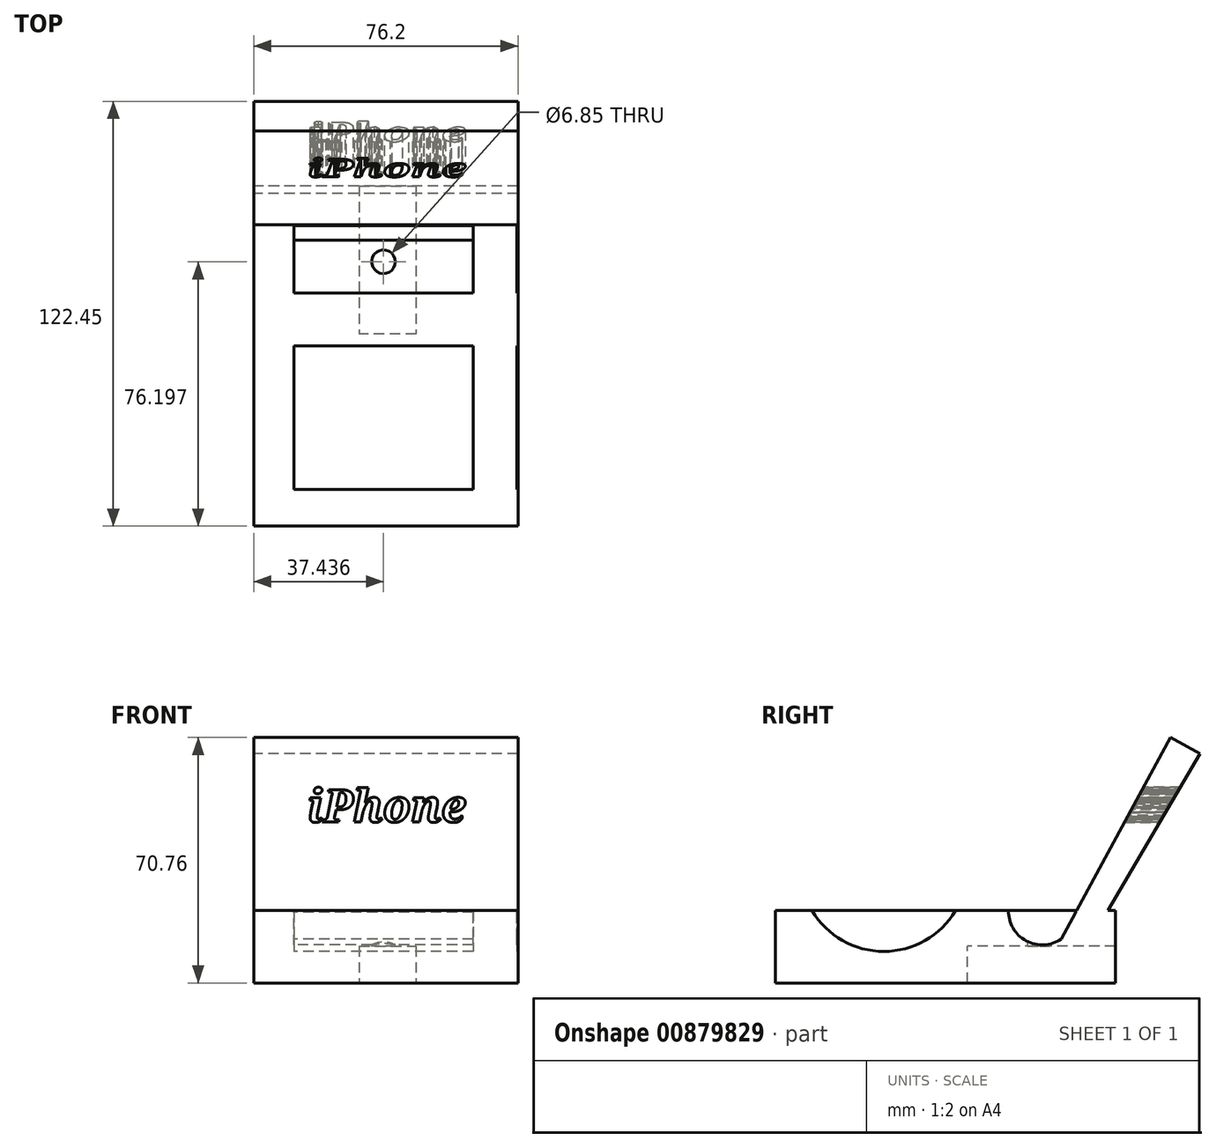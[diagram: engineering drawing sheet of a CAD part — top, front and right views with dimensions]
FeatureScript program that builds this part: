
annotation { "Feature Type Name" : "Feature", "Feature Type Description" : "" }
export const myFeature = defineFeature(function(context is Context, id is Id, definition is map)
    precondition{}
    {
        {
            var Q0;
            Q0=qCreatedBy(makeId("Right.planeOp"),FACE);
            var sketch = newSketch(context, id + "F0", { "sketchPlane" : qUnion([Q0])});
            skLineSegment(sketch, "E0.bottom", {"start": v(42.72, 0) * mm, "end": v(40.53, 0) * mm});
            skLineSegment(sketch, "E0.top", {"start": v(42.72, -20.85) * mm, "end": v(-55.35, -20.85) * mm});
            skLineSegment(sketch, "E0.left", {"start": v(42.72, 0) * mm, "end": v(42.72, -20.85) * mm});
            skLineSegment(sketch, "E0.right", {"start": v(-55.35, 0) * mm, "end": v(-55.35, -20.85) * mm});
            skArc(sketch, "E1", {"start": v(11.9, 0) * mm, "mid": v(16.98, -8.72) * mm, "end": v(27.06, -8.2) * mm});
            skLineSegment(sketch, "E2.trimOffspring", {"start": v(11.9, 0) * mm, "end": v(-3.38, 0) * mm});
            skArc(sketch, "E3", {"start": v(-44.78, 0) * mm, "mid": v(-24.08, -11.77) * mm, "end": v(-3.38, 0) * mm});
            skLineSegment(sketch, "E4", {"start": v(27.06, -8.2) * mm, "end": v(58.58, 49.91) * mm});
            skLineSegment(sketch, "E5", {"start": v(58.58, 49.91) * mm, "end": v(67.1, 45.29) * mm});
            skLineSegment(sketch, "E6", {"start": v(67.1, 45.29) * mm, "end": v(40.53, 0) * mm});
            skArc(sketch, "E7.trimOffspring", {"start": v(31.27, -0.43) * mm, "mid": v(31.27, -0.21) * mm, "end": v(31.27, 0) * mm});
            skLineSegment(sketch, "E8.trimOffspring", {"start": v(31.5, 0) * mm, "end": v(31.27, 0) * mm});
            skLineSegment(sketch, "E9.trimOffspring", {"start": v(-44.78, 0) * mm, "end": v(-55.35, 0) * mm});
            skSolve(sketch);
        }
        {
            var Q0;
            Q0 = qSketchRegion(id + "F0", true);
            extrude(context, id + "F1", {"entities" : qUnion([Q0]), "depth" : 76.2 * mm, "offsetDistance" : 25.4 * mm});
        }
        {
            var Q0;
            Q0=qCreatedBy(makeId("Top.planeOp"),FACE);
            var sketch = newSketch(context, id + "F2", { "sketchPlane" : qUnion([Q0])});
            skLineSegment(sketch, "E10.bottom", {"start": v(0, 32) * mm, "end": v(11.6, 32) * mm});
            skLineSegment(sketch, "E10.top", {"start": v(0, -55.2) * mm, "end": v(11.6, -55.2) * mm});
            skLineSegment(sketch, "E10.left", {"start": v(0, 32) * mm, "end": v(0, -55.2) * mm});
            skLineSegment(sketch, "E10.right", {"start": v(11.6, 32) * mm, "end": v(11.6, -55.2) * mm});
            skLineSegment(sketch, "E11.bottom", {"start": v(75.9, -55.2) * mm, "end": v(63.27, -55.2) * mm});
            skLineSegment(sketch, "E11.top", {"start": v(75.9, 32) * mm, "end": v(63.27, 32) * mm});
            skLineSegment(sketch, "E11.left", {"start": v(75.9, -55.2) * mm, "end": v(75.9, 32) * mm});
            skLineSegment(sketch, "E11.right", {"start": v(63.27, -55.2) * mm, "end": v(63.27, 32) * mm});
            skSolve(sketch);
        }
        {
            var Q0;
            Q0 = qSketchRegion(id + "F2", true);
            extrude(context, id + "F3", {"entities" : qUnion([Q0]), "operationType" : NewBodyOperationType.ADD, "oppositeDirection" : true, "depth" : 20.32 * mm, "offsetDistance" : 25.4 * mm});
        }
        {
            var Q0;
            Q0=qCreatedBy(makeId("Top.planeOp"),FACE);
            var sketch = newSketch(context, id + "F4", { "sketchPlane" : qUnion([Q0])});
            skCircle(sketch, "E12", {"center": v(37.44, 20.85) * mm, "radius": 3.42 * mm});
            skSolve(sketch);
        }
        {
            var Q0;
            Q0 = qSketchRegion(id + "F4", true);
            extrude(context, id + "F5", {"entities" : qUnion([Q0]), "operationType" : NewBodyOperationType.REMOVE, "oppositeDirection" : true, "depth" : 177.8 * mm, "offsetDistance" : 25.4 * mm});
        }
        {
            var Q0;
            Q0=qCreatedBy(makeId("Front.planeOp"),FACE);
            var sketch = newSketch(context, id + "F6", { "sketchPlane" : qUnion([Q0])});
            skText(sketch, "E13", { "text": "iPhone", "fontName": "NotoSerif-BoldItalic.ttf"});
            const initialGuessF6  = {"E13": [0.01541, 0.02554, 1, 0, 0.0094]};
            skSetInitialGuess(sketch, initialGuessF6);
            skSolve(sketch);
        }
        {
            var Q0;
            Q0 = qSketchRegion(id + "F6", true);
            extrude(context, id + "F7", {"entities" : qUnion([Q0]), "operationType" : NewBodyOperationType.REMOVE, "oppositeDirection" : true, "depth" : 203.2 * mm, "offsetDistance" : 25.4 * mm});
        }
        {
            var Q0;
            Q0=qCreatedBy(makeId("Front.planeOp"),FACE);
            var sketch = newSketch(context, id + "F8", { "sketchPlane" : qUnion([Q0])});
            skLineSegment(sketch, "E14.bottom", {"start": v(46.83, -22.9) * mm, "end": v(30.39, -22.9) * mm});
            skLineSegment(sketch, "E14.top", {"start": v(46.83, -10.28) * mm, "end": v(30.39, -10.28) * mm});
            skLineSegment(sketch, "E14.left", {"start": v(46.83, -22.9) * mm, "end": v(46.83, -10.28) * mm});
            skLineSegment(sketch, "E14.right", {"start": v(30.39, -22.9) * mm, "end": v(30.39, -10.28) * mm});
            skSolve(sketch);
        }
        {
            var Q0;
            Q0 = qSketchRegion(id + "F8", true);
            extrude(context, id + "F9", {"entities" : qUnion([Q0]), "operationType" : NewBodyOperationType.REMOVE, "oppositeDirection" : true, "depth" : 76.2 * mm, "offsetDistance" : 25.4 * mm});
        }
    });
